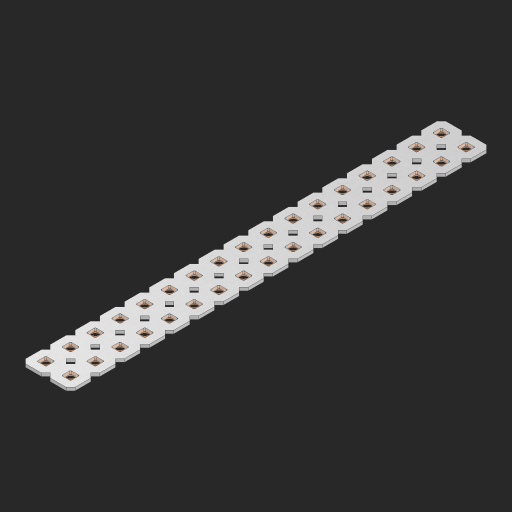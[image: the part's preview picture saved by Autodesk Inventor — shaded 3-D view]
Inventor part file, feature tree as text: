
AUTODESK INVENTOR PART (.ipt)
format: ipt  version: 2023 (Build 270158000, 158)  size: 665,088 bytes
history: native  units: in
note: dims shown in document units (in); Inventor stores cm internally (conversion verified against a paired STEP export)
features: other x35, extrude x33, sketch x2, pattern_linear x1
ambient origin geometry x8: Origin, YZ Plane, XZ Plane, XY Plane, X Axis, Y Axis, Z Axis, Center Point
bodies: Solid1 (feature_tree), Body (feature_tree)
feature tree (71):
  pattern_linear  "Rectangular Pattern1"  Spacing1=0.09in  [1 undecoded]
  sketch  "Sketch1"  dims[d1=0.5in]
  sketch  "Sketch2"  dims[d2=0.182in d3=0.09in d4=0.09in d5=0.09in d6=0.09in d7=0.09in d8=0.09in d9=0.09in d10=0.09in d11=0.02in d13=0.0in d14=0.172in d15=0.0625in d16=0.0in d19=0.5in d22=0.5in]
  other  "Srf1"
  other  "Srf126"
  other  "Srf127"
  other  "Srf128"
  other  "Srf129"
  other  "Srf130"
  other  "Srf131"
  other  "Srf250"
  other  "Srf251"
  other  "Srf252"
  other  "Srf253"
  other  "Srf254"
  other  "Srf255"
  other  "Srf256"
  other  "Srf257"
  other  "Srf258"
  other  "Srf259"
  other  "Srf268"
  other  "Srf269"
  other  "Srf270"
  other  "Srf271"
  other  "Srf272"
  other  "Srf273"
  other  "Srf274"
  other  "Srf275"
  other  "Srf276"
  other  "Srf277"
  other  "Srf278"
  other  "Srf279"
  other  "Srf280"
  other  "Srf281"
  other  "Srf282"
  other  "Srf283"
  other  "Srf284"
  other  "Circle"
  extrude  "ExtrusionSrf126"  Depth=0.09in
  extrude  "ExtrusionSrf127"  Depth=0.09in
  extrude  "ExtrusionSrf128"  Depth=0.09in
  extrude  "ExtrusionSrf129"  Depth=0.09in
  extrude  "ExtrusionSrf130"  Depth=0.09in
  extrude  "ExtrusionSrf131"  Depth=0.09in
  extrude  "ExtrusionSrf250"  Depth=0.09in
  extrude  "ExtrusionSrf251"  Depth=0.02in
  extrude  "ExtrusionSrf252"  TaperAngle=0.0deg  [1 undecoded]
  extrude  "ExtrusionSrf253"  Depth=0.5in
  extrude  "ExtrusionSrf254"  Depth=0.0625in TaperAngle=0.0deg
  extrude  "ExtrusionSrf255"  Depth=0.5in
  extrude  "ExtrusionSrf256"  Depth=0.5in
  extrude  "ExtrusionSrf257"  [1 undecoded]
  extrude  "ExtrusionSrf258"  [1 undecoded]
  extrude  "ExtrusionSrf259"  [1 undecoded]
  extrude  "ExtrusionSrf268"  [1 undecoded]
  extrude  "ExtrusionSrf269"  [1 undecoded]
  extrude  "ExtrusionSrf270"  [1 undecoded]
  extrude  "ExtrusionSrf271"  [1 undecoded]
  extrude  "ExtrusionSrf272"  [1 undecoded]
  extrude  "ExtrusionSrf273"  [1 undecoded]
  extrude  "ExtrusionSrf274"  [1 undecoded]
  extrude  "ExtrusionSrf275"  [1 undecoded]
  extrude  "ExtrusionSrf276"  [1 undecoded]
  extrude  "ExtrusionSrf277"  [1 undecoded]
  extrude  "ExtrusionSrf278"  [1 undecoded]
  extrude  "ExtrusionSrf279"  [1 undecoded]
  extrude  "ExtrusionSrf280"  [1 undecoded]
  extrude  "ExtrusionSrf281"  [1 undecoded]
  extrude  "ExtrusionSrf282"  [1 undecoded]
  extrude  "ExtrusionSrf283"  [1 undecoded]
  extrude  "ExtrusionSrf284"  [1 undecoded]
note: 22 required parameter values undecoded (feature->parameter linkage not recoverable at this tier; creation-order binding heuristic only, values carry confidence <= 0.55)
